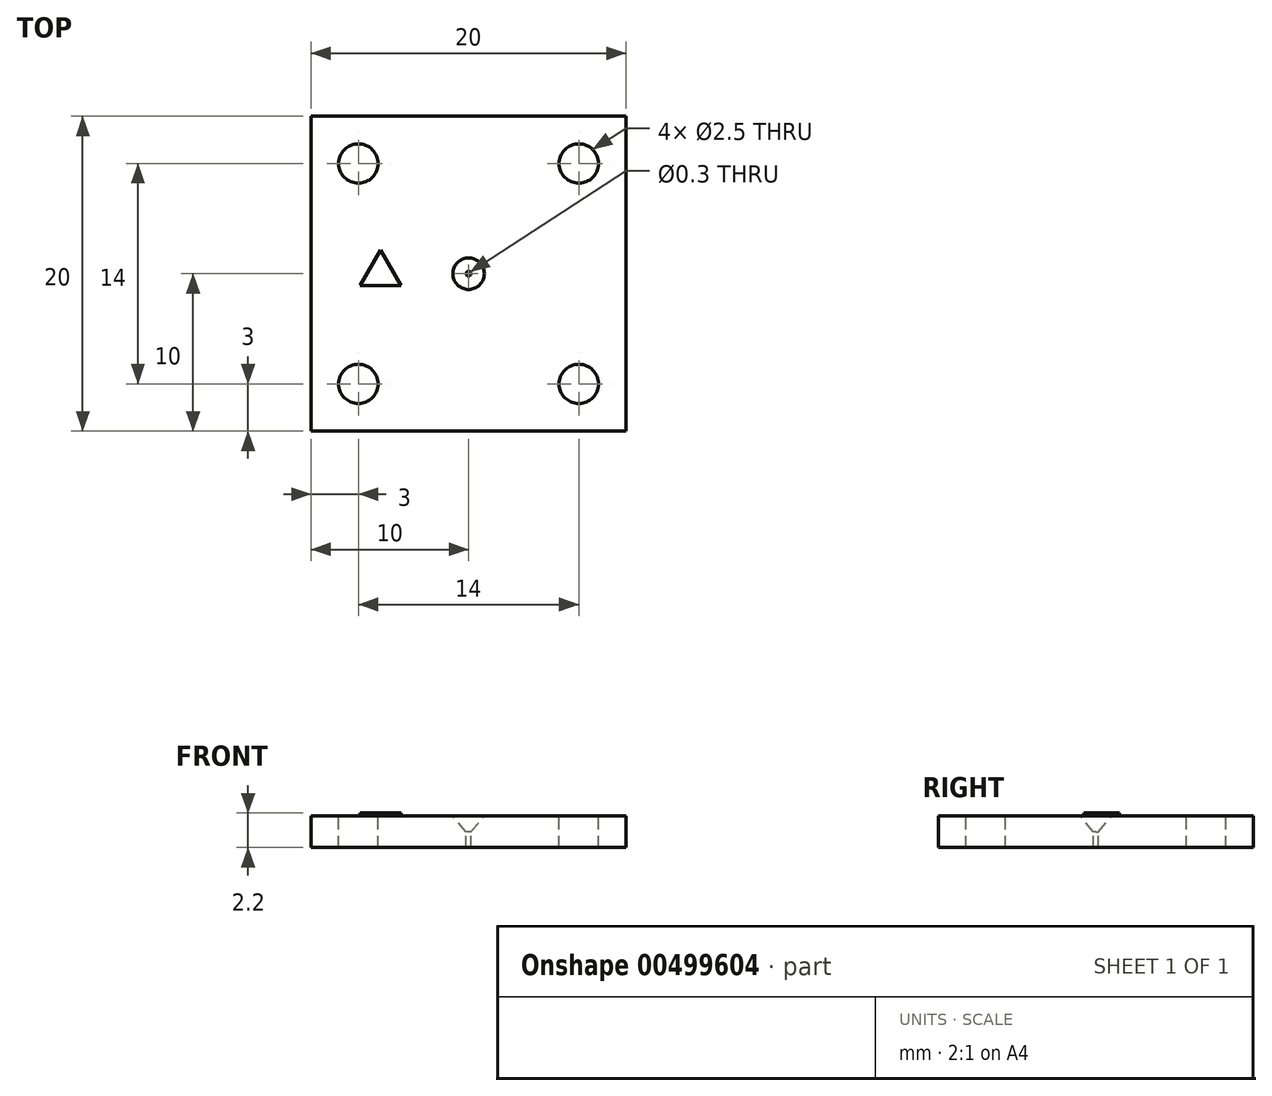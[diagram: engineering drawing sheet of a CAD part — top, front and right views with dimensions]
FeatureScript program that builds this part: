
annotation { "Feature Type Name" : "Feature", "Feature Type Description" : "" }
export const myFeature = defineFeature(function(context is Context, id is Id, definition is map)
    precondition{}
    {
        {
            var Q0;
            Q0=qCreatedBy(makeId("Top.planeOp"),FACE);
            var sketch = newSketch(context, id + "F0", { "sketchPlane" : qUnion([Q0])});
            skLineSegment(sketch, "E0.bottom", {"start": v(-10, 10) * mm, "end": v(10, 10) * mm});
            skLineSegment(sketch, "E0.top", {"start": v(-10, -10) * mm, "end": v(10, -10) * mm});
            skLineSegment(sketch, "E0.left", {"start": v(-10, 10) * mm, "end": v(-10, -10) * mm});
            skLineSegment(sketch, "E0.right", {"start": v(10, 10) * mm, "end": v(10, -10) * mm});
            skSolve(sketch);
        }
        {
            var Q0;
            Q0=makeQuery(id+"F0.imprint","IMPRINT",FACE,{"disambiguationData":[TD([[makeQuery(id+"F0.imprint","IMPRINT",EDGE,{"derivedFrom":sQuery(id+"F0.wireOp",EDGE,"E0.bottom")}),-1.0]])]});
            extrude(context, id + "F1", {"entities" : qUnion([Q0]), "oppositeDirection" : true, "depth" : 1 * mm});
        }
        {
            var Q0;
            Q0=makeQuery(id+"F1.opExtrude","CAP_FACE",FACE,{"disambiguationData":[OSD([sQuery(id+"F0.wireOp",EDGE,"E0.bottom"),sQuery(id+"F0.wireOp",EDGE,"E0.top"),sQuery(id+"F0.wireOp",EDGE,"E0.left"),sQuery(id+"F0.wireOp",EDGE,"E0.right")])],"isStart":true});
            var sketch = newSketch(context, id + "F2", { "sketchPlane" : qUnion([Q0])});
            skCircle(sketch, "E1", {"center": v(0, 0) * mm, "radius": 1 * mm});
            skSolve(sketch);
        }
        {
            var Q0;
            Q0=makeQuery(id+"F1.opExtrude","CAP_FACE",FACE,{"disambiguationData":[OSD([sQuery(id+"F0.wireOp",EDGE,"E0.bottom"),sQuery(id+"F0.wireOp",EDGE,"E0.top"),sQuery(id+"F0.wireOp",EDGE,"E0.left"),sQuery(id+"F0.wireOp",EDGE,"E0.right")])],"isStart":false});
            var sketch = newSketch(context, id + "F3", { "sketchPlane" : qUnion([Q0])});
            skCircle(sketch, "E2", {"center": v(0, 0) * mm, "radius": 0.15 * mm});
            skSolve(sketch);
        }
        {
            var Q1;
            Q1=makeQuery(id+"F2.imprint","IMPRINT",FACE,{"disambiguationData":[TD([[makeQuery(id+"F2.imprint","IMPRINT",EDGE,{"derivedFrom":sQuery(id+"F2.wireOp",EDGE,"E1")}),1.0]])]});
            var Q2;
            Q2=makeQuery(id+"F3.imprint","IMPRINT",FACE,{"disambiguationData":[TD([[makeQuery(id+"F3.imprint","IMPRINT",EDGE,{"derivedFrom":sQuery(id+"F3.wireOp",EDGE,"E2")}),1.0]])]});
            loft(context, id + "F4", {"operationType" : NewBodyOperationType.REMOVE, "sheetProfilesArray" : [{ "sheetProfileEntities" : qUnion([Q1]) }, { "sheetProfileEntities" : qUnion([Q2]) }]});
        }
        {
            var Q0;
            Q0=makeQuery(id+"F2.imprint","IMPRINT",FACE,{"disambiguationData":[TD([[makeQuery(id+"F2.imprint","IMPRINT",EDGE,{"derivedFrom":sQuery(id+"F2.wireOp",EDGE,"E1")}),-1.0]])]});
            var sketch = newSketch(context, id + "F5", { "sketchPlane" : qUnion([Q0])});
            skPoint(sketch, "E3", {"position": v(7, 7) * mm});
            skLineSegment(sketch, "E4", {"start": v(10.77, 0) * mm, "end": v(-10.68, 0) * mm});
            skLineSegment(sketch, "E5", {"start": v(0, -10.66) * mm, "end": v(0, 12.03) * mm});
            skPoint(sketch, "E6.MirrorP", {"position": v(-7, 7) * mm});
            skPoint(sketch, "E7.MirrorP", {"position": v(-7, -7) * mm});
            skPoint(sketch, "E8.MirrorP", {"position": v(7, -7) * mm});
            skSolve(sketch);
        }
        {
            var Q0;
            Q0=makeQuery(id+"F3.imprint","IMPRINT",FACE,{"disambiguationData":[TD([[makeQuery(id+"F3.imprint","IMPRINT",EDGE,{"derivedFrom":sQuery(id+"F3.wireOp",EDGE,"E2")}),-1.0]])]});
            var sketch = newSketch(context, id + "F6", { "sketchPlane" : qUnion([Q0])});
            skLineSegment(sketch, "E9.bottom", {"start": v(-10, 10) * mm, "end": v(10, 10) * mm});
            skLineSegment(sketch, "E9.top", {"start": v(-10, -10) * mm, "end": v(10, -10) * mm});
            skLineSegment(sketch, "E9.left", {"start": v(-10, 10) * mm, "end": v(-10, -10) * mm});
            skLineSegment(sketch, "E9.right", {"start": v(10, 10) * mm, "end": v(10, -10) * mm});
            skPoint(sketch, "E9.middle", {"position": v(0, 0) * mm});
            skCircle(sketch, "E10.0", {"center": v(0, 0) * mm, "radius": 0.15 * mm});
            skSolve(sketch);
        }
        {
            var Q0;
            Q0=makeQuery(id+"F6.imprint","IMPRINT",FACE,{"disambiguationData":[TD([[makeQuery(id+"F6.imprint","IMPRINT",EDGE,{"derivedFrom":sQuery(id+"F6.wireOp",EDGE,"E9.bottom")}),-1.0]])]});
            extrude(context, id + "F7", {"entities" : qUnion([Q0]), "operationType" : NewBodyOperationType.ADD, "depth" : 1 * mm});
        }
        {
            var Q0;
            Q0=sQuery(id+"F5.wireOp",VERTEX,"E7.MirrorP");
            var Q1;
            Q1=sQuery(id+"F5.wireOp",VERTEX,"E8.MirrorP");
            var Q2;
            Q2=sQuery(id+"F5.wireOp",VERTEX,"E3");
            var Q3;
            Q3=sQuery(id+"F5.wireOp",VERTEX,"E6.MirrorP");
            var Q4;
            Q4=makeQuery(id+"F1.opExtrude","SWEPT_BODY",BODY,{"disambiguationData":[OSD([sQuery(id+"F0.wireOp",EDGE,"E0.bottom"),sQuery(id+"F0.wireOp",EDGE,"E0.top"),sQuery(id+"F0.wireOp",EDGE,"E0.left"),sQuery(id+"F0.wireOp",EDGE,"E0.right")])]});
            hole(context, id + "F8", {"style" : HoleStyle.SIMPLE, "endStyle" : HoleEndStyle.THROUGH, "standardTappedOrClearance" : lookupTablePath({ "standard" : "ISO", "engagement" : "75%", "pitch" : "0.5 mm", "size" : "M3", "type" : "Tapped" }), "standardBlindInLast" : lookupTablePath({ "standard" : "ISO", "engagement" : "75%", "pitch" : "0.5 mm", "size" : "M3", "type" : "Tapped" }), "holeDiameter" : 2.5 * mm, "showTappedDepth" : true, "isTappedThrough" : true, "tappedDepth" : 12 * mm, "tapClearance" : 3, "startFromSketch" : true, "locations" : qUnion([Q0, Q1, Q2, Q3]), "scope" : qUnion([Q4]), "majorDiameter" : 3 * mm});
        }
        {
            var Q0;
            Q0=makeQuery(id+"F2.imprint","IMPRINT",FACE,{"disambiguationData":[TD([[makeQuery(id+"F2.imprint","IMPRINT",EDGE,{"derivedFrom":sQuery(id+"F2.wireOp",EDGE,"E1")}),-1.0]])]});
            var sketch = newSketch(context, id + "F9", { "sketchPlane" : qUnion([Q0])});
            skCircle(sketch, "E11.cCircle", {"center": v(-5.6, 0) * mm, "radius": 1.5 * mm, "construction": true});
            skLineSegment(sketch, "E11.0", {"start": v(-5.6, 1.5) * mm, "end": v(-4.3, -0.75) * mm});
            skLineSegment(sketch, "E11.1", {"start": v(-4.3, -0.75) * mm, "end": v(-6.9, -0.75) * mm});
            skLineSegment(sketch, "E11.2", {"start": v(-6.9, -0.75) * mm, "end": v(-5.6, 1.5) * mm});
            skSolve(sketch);
        }
        {
            var Q0;
            Q0 = qSketchRegion(id + "F9", true);
            extrude(context, id + "F10", {"entities" : qUnion([Q0]), "operationType" : NewBodyOperationType.ADD, "depth" : .2 * mm, "offsetDistance" : 25 * mm});
        }
    });
